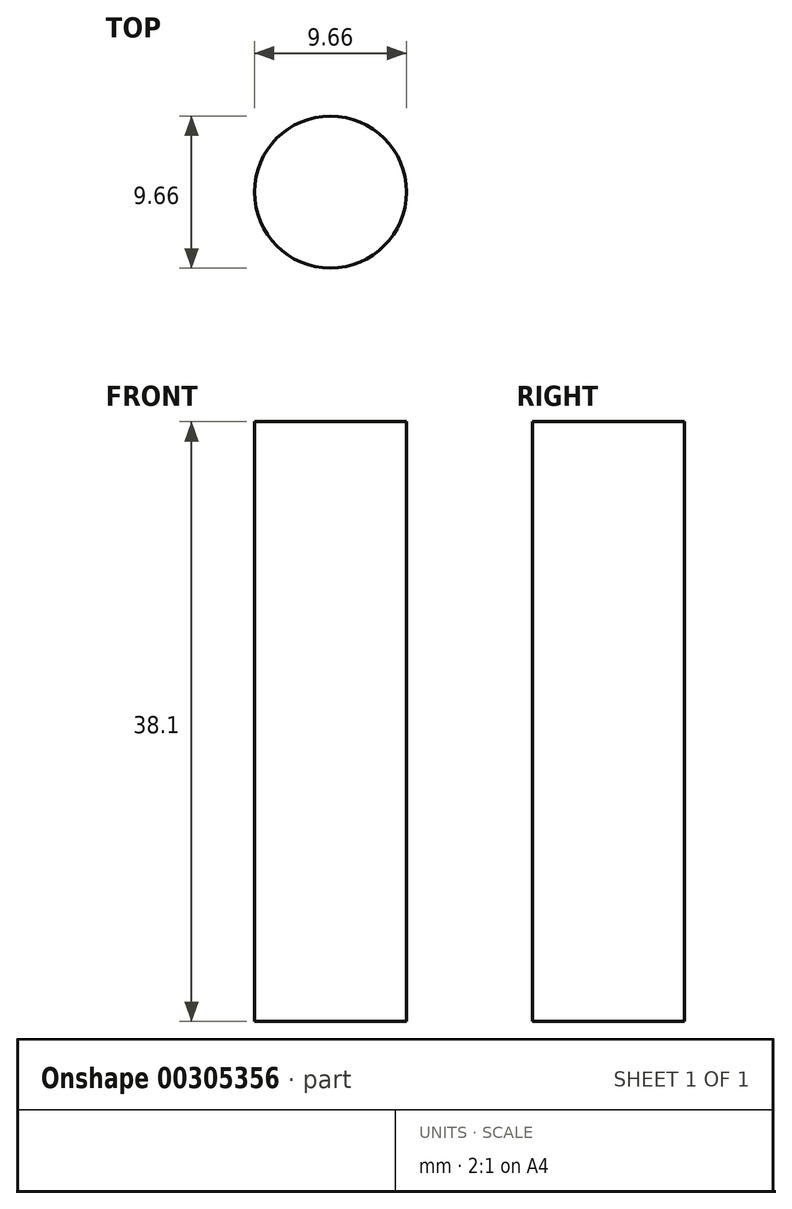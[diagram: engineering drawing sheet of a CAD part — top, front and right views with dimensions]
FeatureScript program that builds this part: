
annotation { "Feature Type Name" : "Feature", "Feature Type Description" : "" }
export const myFeature = defineFeature(function(context is Context, id is Id, definition is map)
    precondition{}
    {
        {
            var Q0;
            Q0=qCreatedBy(makeId("Top.planeOp"),FACE);
            var sketch = newSketch(context, id + "F0", { "sketchPlane" : qUnion([Q0])});
            skCircle(sketch, "E0", {"center": v(0, 0) * mm, "radius": 4.83 * mm});
            skSolve(sketch);
        }
        {
            var Q0;
            Q0=makeQuery(id+"F0.imprint","IMPRINT",FACE,{"disambiguationData":[TD([[makeQuery(id+"F0.imprint","IMPRINT",EDGE,{"derivedFrom":sQuery(id+"F0.wireOp",EDGE,"E0")}),1.0]])]});
            extrude(context, id + "F1", {"entities" : qUnion([Q0]), "depth" : 38.1 * mm});
        }
    });
